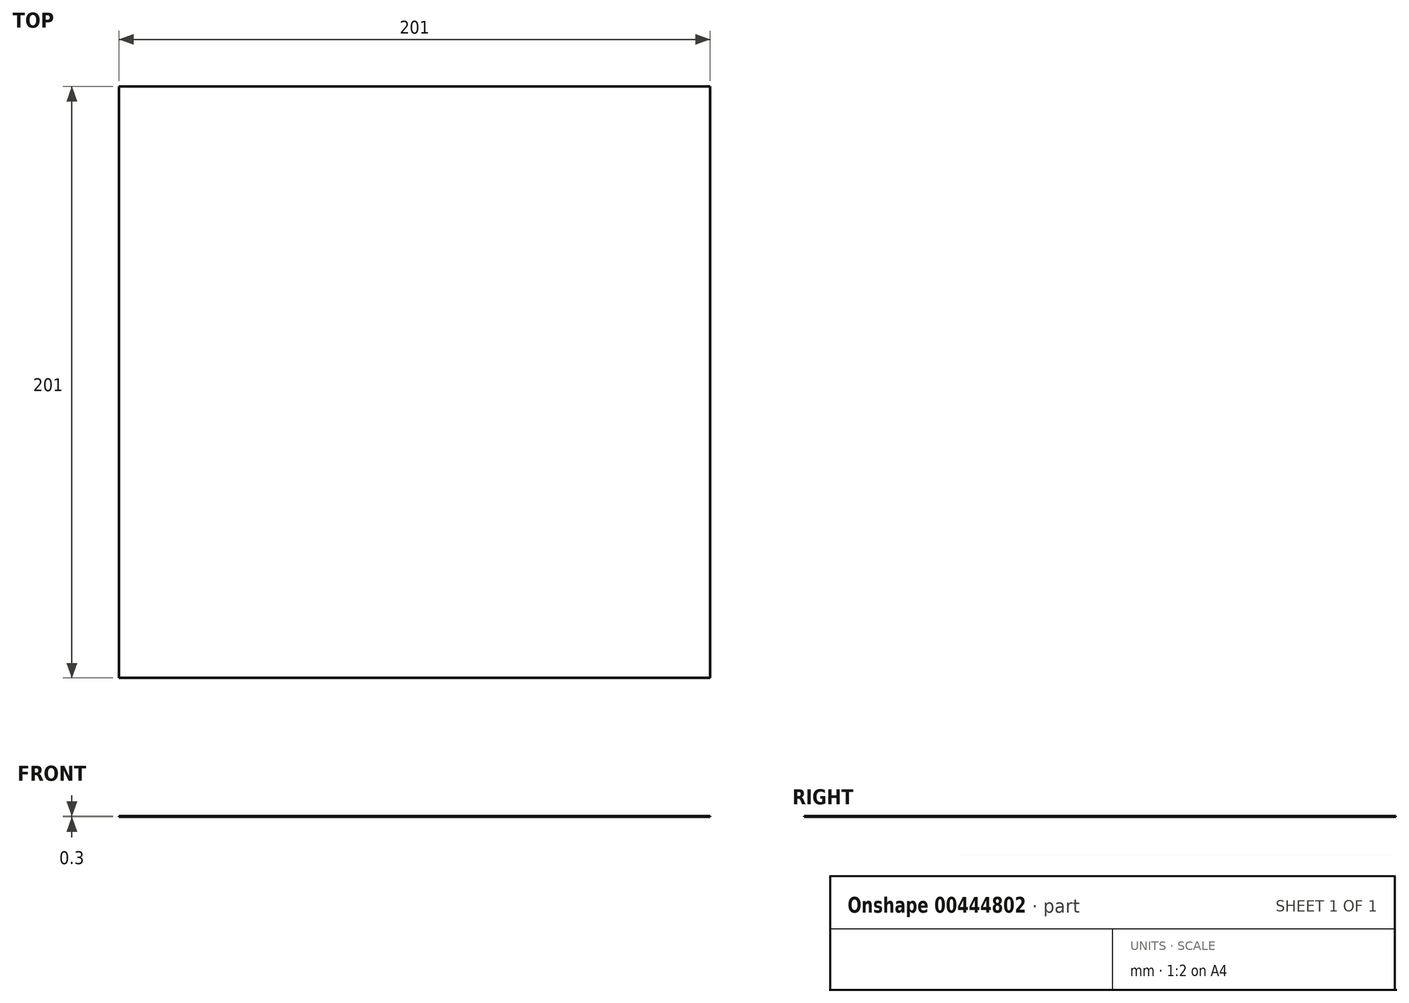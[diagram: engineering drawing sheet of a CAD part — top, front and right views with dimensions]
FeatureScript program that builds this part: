
annotation { "Feature Type Name" : "Feature", "Feature Type Description" : "" }
export const myFeature = defineFeature(function(context is Context, id is Id, definition is map)
    precondition{}
    {
        {
            var Q0;
            Q0=qCreatedBy(makeId("Top.planeOp"),FACE);
            var sketch = newSketch(context, id + "F0", { "sketchPlane" : qUnion([Q0])});
            skLineSegment(sketch, "E0.bottom", {"start": v(100.5, 100.5) * mm, "end": v(-100.5, 100.5) * mm});
            skLineSegment(sketch, "E0.top", {"start": v(100.5, -100.5) * mm, "end": v(-100.5, -100.5) * mm});
            skLineSegment(sketch, "E0.left", {"start": v(100.5, 100.5) * mm, "end": v(100.5, -100.5) * mm});
            skLineSegment(sketch, "E0.right", {"start": v(-100.5, 100.5) * mm, "end": v(-100.5, -100.5) * mm});
            skPoint(sketch, "E0.middle", {"position": v(0, 0) * mm});
            skSolve(sketch);
        }
        {
            var Q0;
            Q0=makeQuery(id+"F0.imprint","IMPRINT",FACE,{"disambiguationData":[TD([[makeQuery(id+"F0.imprint","IMPRINT",EDGE,{"derivedFrom":sQuery(id+"F0.wireOp",EDGE,"E0.bottom")}),1.0]])]});
            extrude(context, id + "F1", {"entities" : qUnion([Q0]), "depth" : 0.3 * mm});
        }
    });
